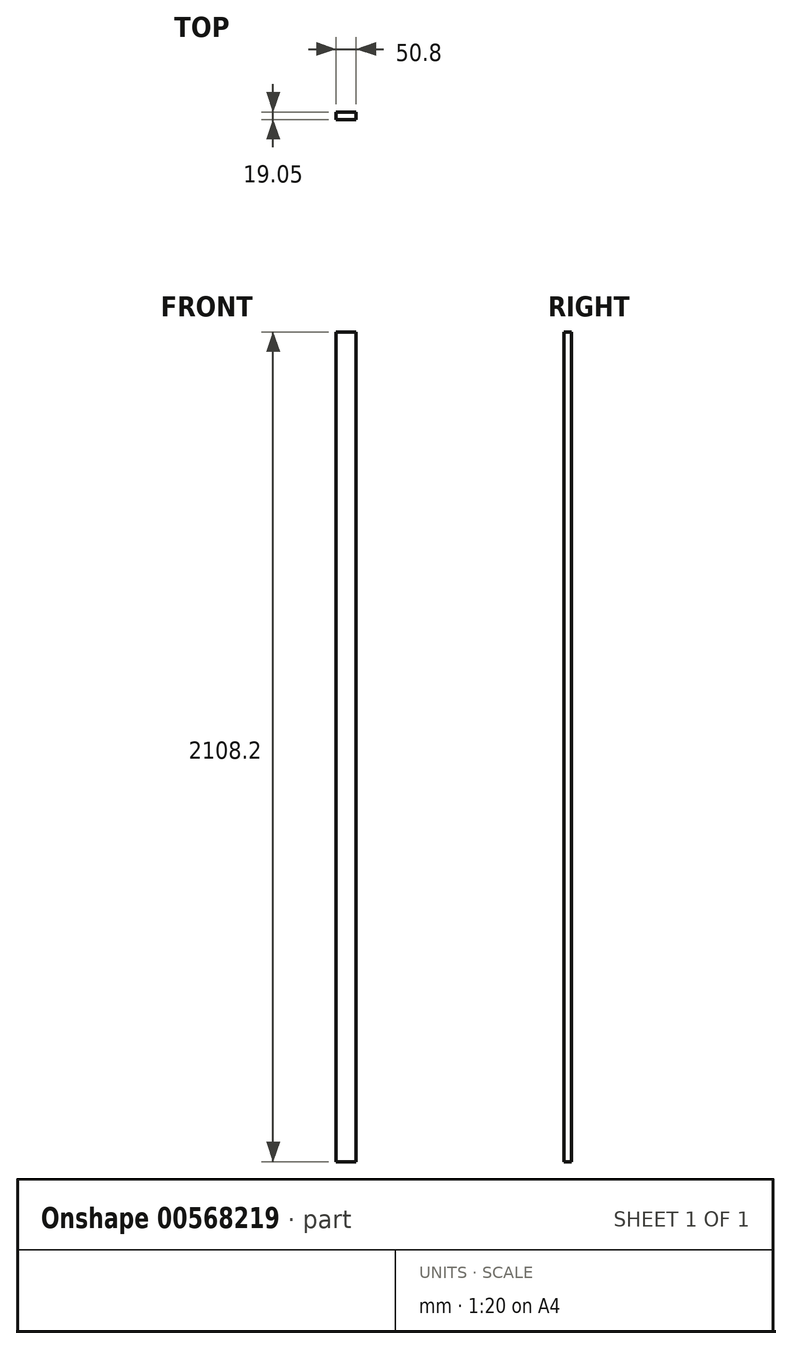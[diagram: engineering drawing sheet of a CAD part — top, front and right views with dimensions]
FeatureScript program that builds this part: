
annotation { "Feature Type Name" : "Feature", "Feature Type Description" : "" }
export const myFeature = defineFeature(function(context is Context, id is Id, definition is map)
    precondition{}
    {
        {
            var Q0;
            Q0=qCreatedBy(makeId("Front.planeOp"),FACE);
            var sketch = newSketch(context, id + "F0", { "sketchPlane" : qUnion([Q0])});
            skLineSegment(sketch, "E0.bottom", {"start": v(0, 0) * mm, "end": v(50.8, 0) * mm});
            skLineSegment(sketch, "E0.top", {"start": v(0, 2108.2) * mm, "end": v(50.8, 2108.2) * mm});
            skLineSegment(sketch, "E0.left", {"start": v(0, 0) * mm, "end": v(0, 2108.2) * mm});
            skLineSegment(sketch, "E0.right", {"start": v(50.8, 0) * mm, "end": v(50.8, 2108.2) * mm});
            skSolve(sketch);
        }
        {
            var Q0;
            Q0=makeQuery(id+"F0.imprint","IMPRINT",FACE,{"disambiguationData":[TD([[makeQuery(id+"F0.imprint","IMPRINT",EDGE,{"derivedFrom":sQuery(id+"F0.wireOp",EDGE,"E0.bottom")}),1.0]])]});
            extrude(context, id + "F1", {"entities" : qUnion([Q0]), "depth" : 19.05 * mm, "offsetDistance" : 25.4 * mm});
        }
    });
